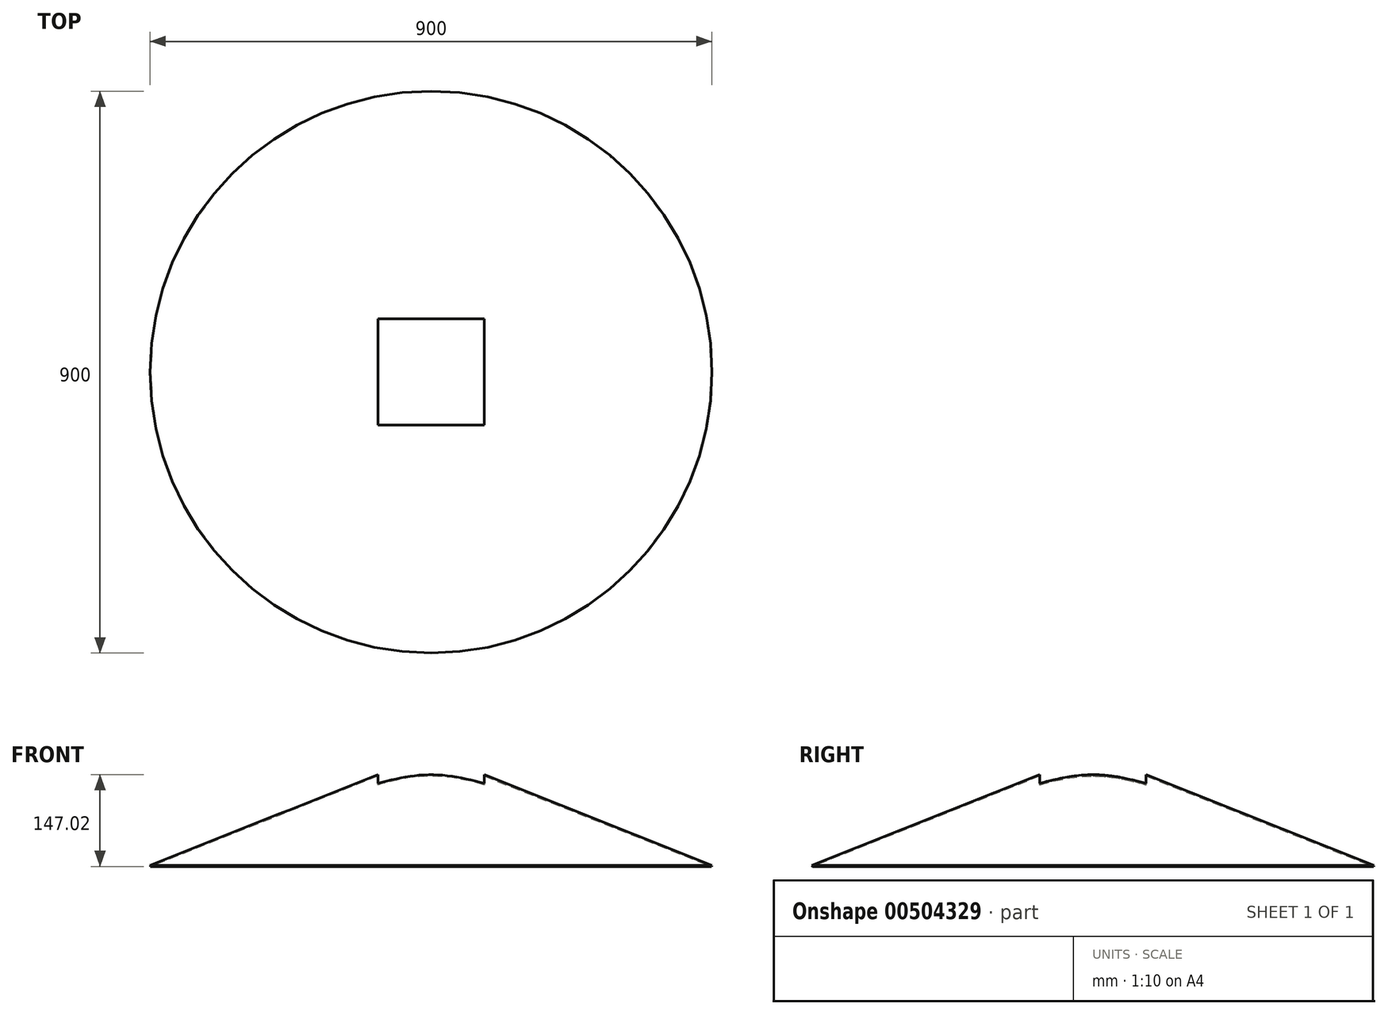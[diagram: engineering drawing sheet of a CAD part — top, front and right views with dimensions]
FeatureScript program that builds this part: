
annotation { "Feature Type Name" : "Feature", "Feature Type Description" : "" }
export const myFeature = defineFeature(function(context is Context, id is Id, definition is map)
    precondition{}
    {
        {
            var Q0;
            Q0=qCreatedBy(makeId("Front.planeOp"),FACE);
            var sketch = newSketch(context, id + "F0", { "sketchPlane" : qUnion([Q0])});
            skLineSegment(sketch, "E0", {"start": v(0, 0) * mm, "end": v(0, 114.12) * mm, "construction": true});
            skLineSegment(sketch, "E1", {"start": v(0, 77.1) * mm, "end": v(450, -101.87) * mm});
            skLineSegment(sketch, "E2.0", {"start": v(0, 74.95) * mm, "end": v(449.26, -103.73) * mm});
            skLineSegment(sketch, "E3", {"start": v(449.26, -103.73) * mm, "end": v(450, -101.87) * mm});
            skLineSegment(sketch, "E4", {"start": v(0, 77.1) * mm, "end": v(0, 74.95) * mm});
            skSolve(sketch);
        }
        {
            var Q0;
            Q0 = qSketchRegion(id + "F0", true);
            var Q1;
            Q1=sQuery(id+"F0.wireOp",EDGE,"E0");
            revolve(context, id + "F1", {"entities" : qUnion([Q0]), "axis" : qUnion([Q1]), "revolveType" : RevolveType.FULL});
        }
        {
            var Q0;
            Q0=qCreatedBy(makeId("Top.planeOp"),FACE);
            var sketch = newSketch(context, id + "F2", { "sketchPlane" : qUnion([Q0])});
            skLineSegment(sketch, "E5.bottom", {"start": v(85, -85) * mm, "end": v(-85, -85) * mm});
            skLineSegment(sketch, "E5.top", {"start": v(85, 85) * mm, "end": v(-85, 85) * mm});
            skLineSegment(sketch, "E5.left", {"start": v(85, -85) * mm, "end": v(85, 85) * mm});
            skLineSegment(sketch, "E5.right", {"start": v(-85, -85) * mm, "end": v(-85, 85) * mm});
            skPoint(sketch, "E5.middle", {"position": v(0, 0) * mm});
            skSolve(sketch);
        }
        {
            var Q0;
            Q0 = qSketchRegion(id + "F2", true);
            var Q1;
            Q1=makeQuery(id+"F1.opRevolve","SWEPT_FACE",FACE,{"disambiguationData":[OSD([sQuery(id+"F0.wireOp",EDGE,"E1")])]});
            extrude(context, id + "F3", {"entities" : qUnion([Q0]), "operationType" : NewBodyOperationType.REMOVE, "endBound" : BoundingType.UP_TO_SURFACE, "endBoundEntityFace" : qUnion([Q1]), "depth" : 25 * mm});
        }
    });
